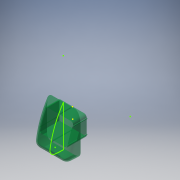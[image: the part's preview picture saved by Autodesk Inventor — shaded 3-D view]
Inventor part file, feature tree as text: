
AUTODESK INVENTOR PART (.ipt)
format: ipt  version: 2018 (Build 220112000, 112)  size: 485,888 bytes
history: native  units: in
note: dims shown in document units (in); Inventor stores cm internally (conversion verified against a paired STEP export)
features: sketch x8, extrude x6, fillet x2, shell x2, plane x1
ambient origin geometry x8: Origin, YZ Plane, XZ Plane, XY Plane, X Axis, Y Axis, Z Axis, Center Point
bodies: Solid1 (feature_tree)
feature tree (19):
  plane  "Work Plane1"
  extrude  "Extrusion1"  Depth=2.55in TaperAngle=0.0deg
  fillet  "Fillet1"  Radius=0.5in
  shell  "Shell1"  Thickness=0.07in
  sketch  "Sketch3"  dims[d3=-0.0175in d11=2.55in d12=0.0in d13=0.5in d14=0.07in]
  sketch  "Sketch4"  dims[d33=1.5in d36=0.0in d37=0.0in d38=0.1in d39=0.2in]
  sketch  "Sketch5"  dims[d40=0.05in d41=0.05in]
  extrude  "Extrusion4"  TaperAngle=0.0deg  [1 undecoded]
  shell  "Shell3"  Thickness=0.1in
  fillet  "Fillet3"  Radius=0.2in
  sketch  "Sketch6"  dims[d42=0.0in d43=0.0in d51=0.05in d52=0.05in d54=0.0in d55=0.0in]
  extrude  "Extrusion5"  Depth=0.05in
  extrude  "Extrusion8"  Depth=0.05in TaperAngle=0.0deg
  sketch  "Sketch7"  dims[d56=0.05in d57=90.0deg]
  sketch  "Sketch11"  dims[d60=0.05in]
  sketch  "Sketch10"  dims[d58=0.05in d59=90.0deg]
  sketch  "Sketch12"  dims[d63=1.0in d64=0.0in d67=0.05in d68=0.05in d69=0.05in d71=0.0in d72=1.0in d76=0.05in d77=90.0deg d78=0.05in d79=0.0in]
  extrude  "Extrusion7"  TaperAngle=90.0deg  [1 undecoded]
  extrude  "Extrusion9"  TaperAngle=90.0deg  [1 undecoded]
note: 3 required parameter values undecoded (feature->parameter linkage not recoverable at this tier; creation-order binding heuristic only, values carry confidence <= 0.55)
